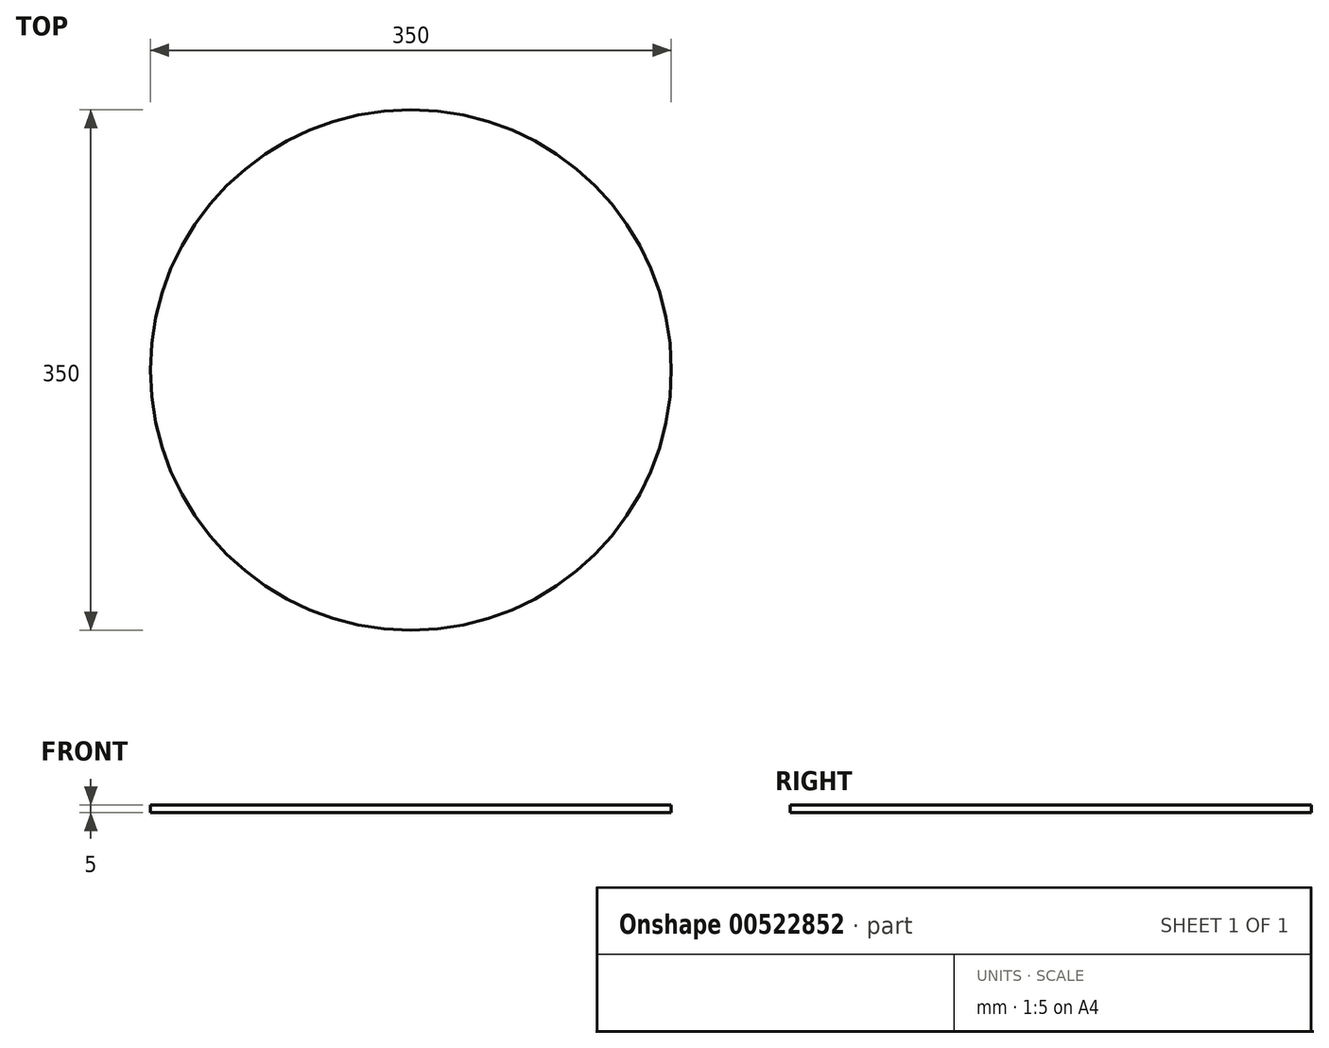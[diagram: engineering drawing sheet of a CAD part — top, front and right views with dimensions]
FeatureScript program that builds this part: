
annotation { "Feature Type Name" : "Feature", "Feature Type Description" : "" }
export const myFeature = defineFeature(function(context is Context, id is Id, definition is map)
    precondition{}
    {
        {
            var Q0;
            Q0=qCreatedBy(makeId("Top.planeOp"),FACE);
            var sketch = newSketch(context, id + "F0", { "sketchPlane" : qUnion([Q0])});
            skCircle(sketch, "E0", {"center": v(0, 0) * mm, "radius": 175 * mm});
            skSolve(sketch);
        }
        {
            var Q0;
            Q0=makeQuery(id+"F0.imprint","IMPRINT",FACE,{"disambiguationData":[TD([[makeQuery(id+"F0.imprint","IMPRINT",EDGE,{"derivedFrom":sQuery(id+"F0.wireOp",EDGE,"E0")}),1.0]])]});
            extrude(context, id + "F1", {"entities" : qUnion([Q0]), "depth" : 5 * mm, "offsetDistance" : 25 * mm});
        }
    });
